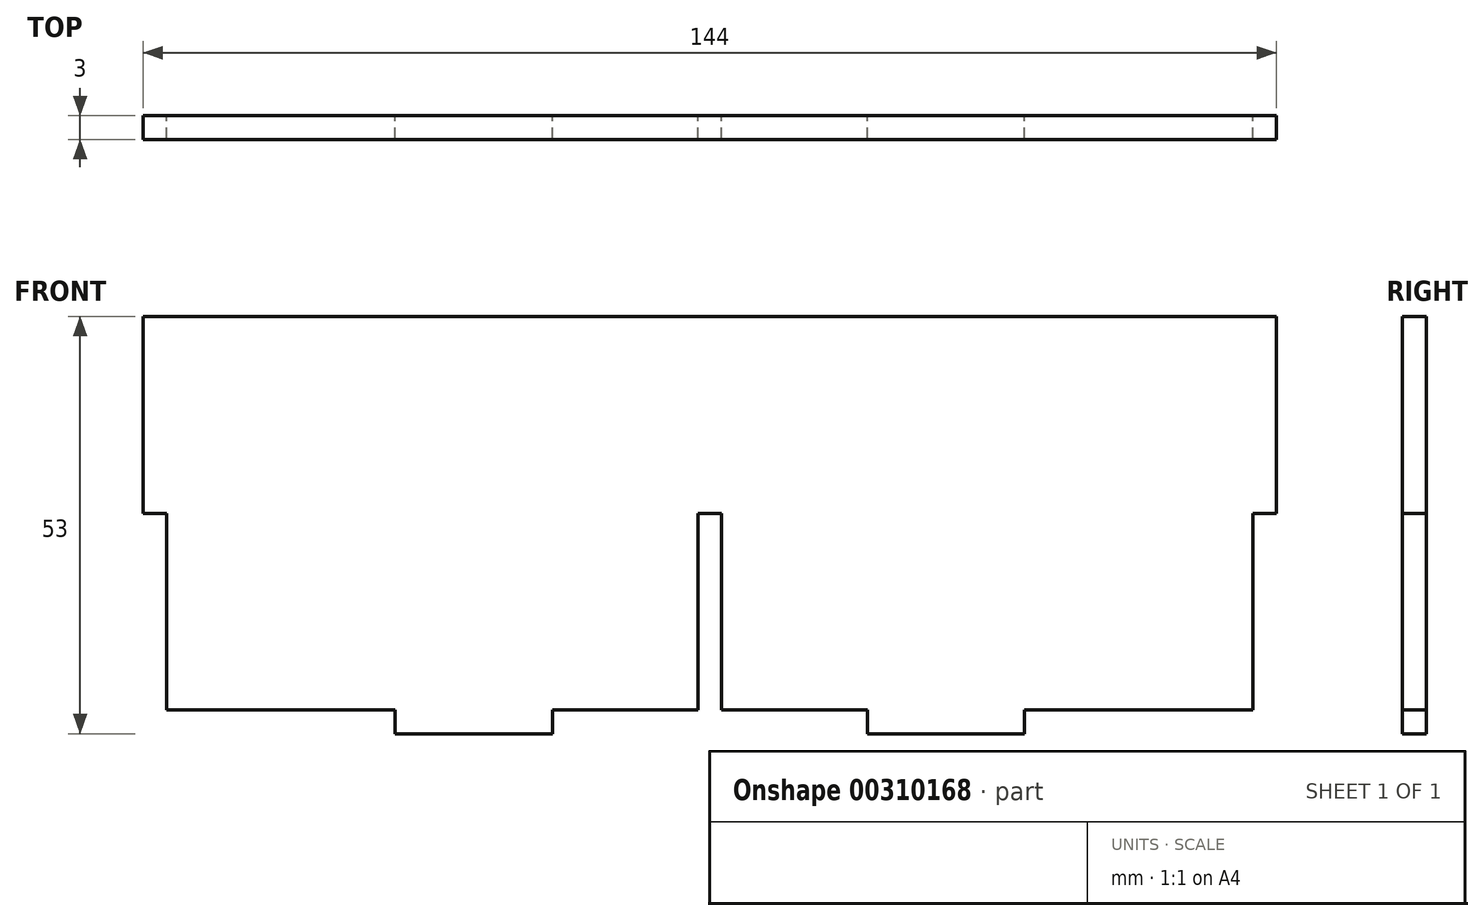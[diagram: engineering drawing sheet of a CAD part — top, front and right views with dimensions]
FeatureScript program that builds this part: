
annotation { "Feature Type Name" : "Feature", "Feature Type Description" : "" }
export const myFeature = defineFeature(function(context is Context, id is Id, definition is map)
    precondition{}
    {
        {
            var Q0;
            Q0=qCreatedBy(makeId("Front.planeOp"),FACE);
            var sketch = newSketch(context, id + "F0", { "sketchPlane" : qUnion([Q0])});
            skLineSegment(sketch, "E0.bottom", {"start": v(69, -25) * mm, "end": v(40, -25) * mm});
            skLineSegment(sketch, "E0.top", {"start": v(72, 25) * mm, "end": v(-72, 25) * mm});
            skLineSegment(sketch, "E0.left", {"start": v(72, 0) * mm, "end": v(72, 25) * mm});
            skLineSegment(sketch, "E0.right", {"start": v(-72, 0) * mm, "end": v(-72, 25) * mm});
            skPoint(sketch, "E0.middle", {"position": v(0, 0) * mm});
            skLineSegment(sketch, "E1.top", {"start": v(-20, -28) * mm, "end": v(-40, -28) * mm});
            skLineSegment(sketch, "E1.left", {"start": v(-20, -25) * mm, "end": v(-20, -28) * mm});
            skLineSegment(sketch, "E1.right", {"start": v(-40, -25) * mm, "end": v(-40, -28) * mm});
            skLineSegment(sketch, "E2.top", {"start": v(-72, 0) * mm, "end": v(-69, 0) * mm});
            skLineSegment(sketch, "E2.right", {"start": v(-69, -25) * mm, "end": v(-69, 0) * mm});
            skPoint(sketch, "E3.orphan", {"position": v(-72, -25) * mm});
            skLineSegment(sketch, "E4.trimOffspring", {"start": v(-40, -25) * mm, "end": v(-69, -25) * mm});
            skLineSegment(sketch, "E5.MirrorCS", {"start": v(69, -25) * mm, "end": v(69, 0) * mm});
            skLineSegment(sketch, "E6.MirrorCS", {"start": v(72, 0) * mm, "end": v(69, 0) * mm});
            skLineSegment(sketch, "E7.MirrorCS", {"start": v(20, -28) * mm, "end": v(40, -28) * mm});
            skLineSegment(sketch, "E8.MirrorCS", {"start": v(20, -25) * mm, "end": v(20, -28) * mm});
            skLineSegment(sketch, "E9.MirrorCS", {"start": v(40, -25) * mm, "end": v(40, -28) * mm});
            skLineSegment(sketch, "E10.trimOffspring", {"start": v(20, -25) * mm, "end": v(1.5, -25) * mm});
            skPoint(sketch, "E11.orphan", {"position": v(72, -25) * mm});
            skLineSegment(sketch, "E12.top", {"start": v(1.5, 0) * mm, "end": v(-1.5, 0) * mm});
            skLineSegment(sketch, "E12.left", {"start": v(1.5, -25) * mm, "end": v(1.5, 0) * mm});
            skLineSegment(sketch, "E12.right", {"start": v(-1.5, -25) * mm, "end": v(-1.5, 0) * mm});
            skLineSegment(sketch, "E13.trimOffspring", {"start": v(-1.5, -25) * mm, "end": v(-20, -25) * mm});
            skSolve(sketch);
        }
        {
            var Q0;
            Q0 = qSketchRegion(id + "F0", true);
            extrude(context, id + "F1", {"entities" : qUnion([Q0]), "depth" : 3 * mm});
        }
    });
